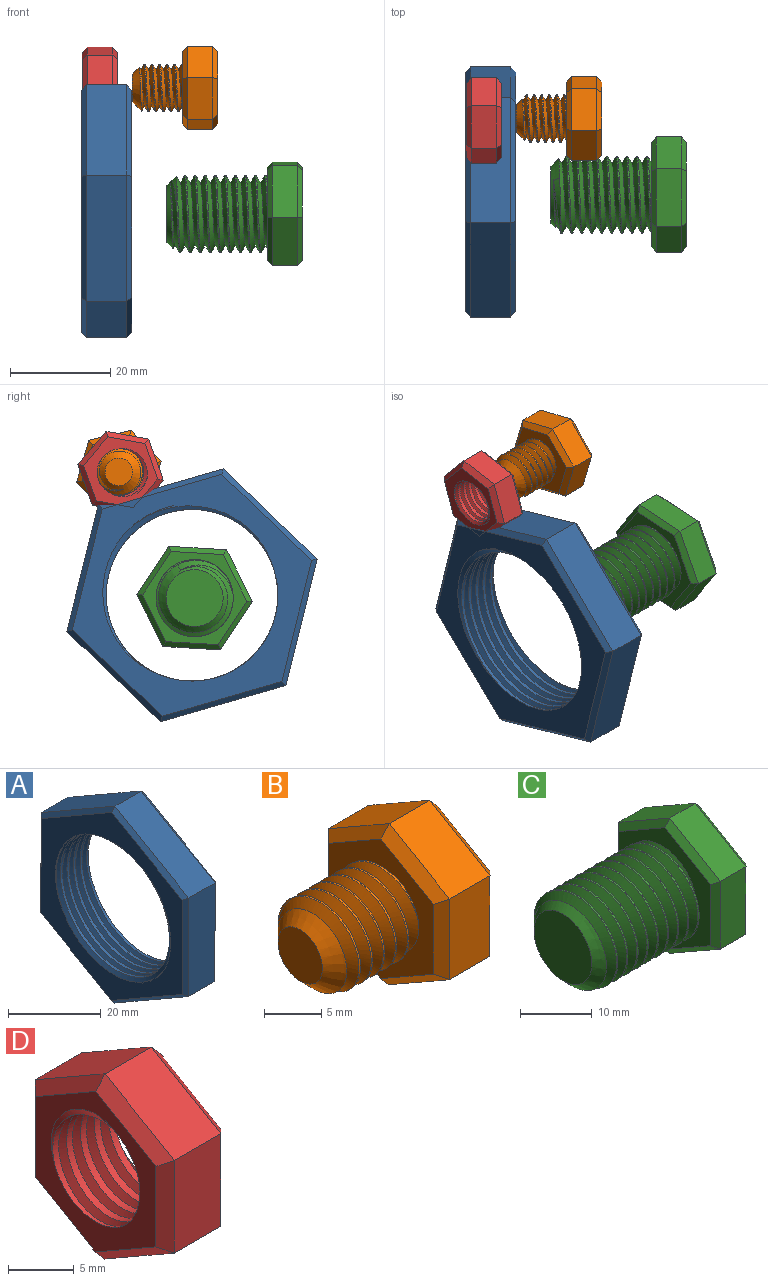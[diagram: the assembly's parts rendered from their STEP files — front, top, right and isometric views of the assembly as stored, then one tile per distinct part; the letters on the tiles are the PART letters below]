
ASSEMBLY  parts=4 mates=2
PART A: 23 faces, bbox 11.6x45x52 mm
  f0: cylinder r=17.12mm len=34.24mm, axis (1,0,0), area 378.5mm2, adj f7,f8,f21,f22
  f1: plane 22.48x13.02mm, normal (0,-0.5,0.87), area 207.8mm2, adj f2,f6,f14,f18
  f2: plane 25.98x8mm, normal (0,-1,0), area 207.8mm2, adj f1,f3,f12,f16
  f3: plane 22.52x12.96mm, normal (0,-0.5,-0.87), area 207.8mm2, adj f2,f4,f10,f15
  f4: plane 22.48x13.02mm, normal (0,0.5,-0.87), area 207.8mm2, adj f3,f5,f9,f17
  f5: plane 25.98x8mm, normal (0,1,0), area 207.8mm2, adj f4,f6,f11,f19
  f6: plane 22.52x12.96mm, normal (0,0.5,0.87), area 207.8mm2, adj f1,f5,f13,f20
  f7: plane 49.65x43.04mm, normal (-1,0,0), area 640.6mm2, adj f0,f9,f10,f11,f12,f13,f14,f21
  f8: plane 49.65x43.04mm, normal (1,0,0), area 640.6mm2, adj f0,f15,f16,f17,f18,f19,f20,f21
  f9: plane 22.48x13.6mm, normal (-0.71,0.35,-0.61), area 35.9mm2, adj f4,f7,f10,f11
  f10: plane 22.52x13.54mm, normal (-0.71,-0.35,-0.61), area 35.9mm2, adj f3,f7,f9,f12
  f11: plane 25.98x1.04mm, normal (-0.71,0.71,0), area 35.9mm2, adj f5,f7,f9,f13
  f12: plane 25.98x1.04mm, normal (-0.71,-0.71,0), area 35.9mm2, adj f2,f7,f10,f14
  f13: plane 22.52x13.54mm, normal (-0.71,0.35,0.61), area 35.9mm2, adj f6,f7,f11,f14
  f14: plane 22.48x13.6mm, normal (-0.71,-0.35,0.61), area 35.9mm2, adj f1,f7,f12,f13
  f15: plane 22.52x13.54mm, normal (0.71,-0.35,-0.61), area 35.9mm2, adj f3,f8,f16,f17
  f16: plane 25.98x1.04mm, normal (0.71,-0.71,0), area 35.9mm2, adj f2,f8,f15,f18
  f17: plane 22.48x13.6mm, normal (0.71,0.35,-0.61), area 35.9mm2, adj f4,f8,f15,f19
  f18: plane 22.48x13.6mm, normal (0.71,-0.35,0.61), area 35.9mm2, adj f1,f8,f16,f20
  f19: plane 25.98x1.04mm, normal (0.71,0.71,0), area 35.9mm2, adj f5,f8,f17,f20
  f20: plane 22.52x13.54mm, normal (0.71,0.35,0.61), area 35.9mm2, adj f6,f8,f18,f19
  f21: bspline ~42.13x36.49mm, area 721.4mm2, adj f0,f7,f8,f22
  f22: bspline ~42.13x36.49mm, area 721mm2, adj f0,f7,f8,f21
PART B: 25 faces, bbox 17.8x15.9x18.1 mm
  f0: cylinder r=4.75mm len=9.5mm, axis (1,0,0), area 28.1mm2, adj f1,f2,f4,f12
  f1: bspline ~10.97x9.91mm, area 196.7mm2, adj f0,f2,f4,f12
  f2: bspline ~10.97x10.66mm, area 196.6mm2, adj f0,f1,f4,f12
  f3: plane 5.5x5.5mm, normal (-1,0,0), area 23.8mm2, adj f4
  f4: cone r=4.75mm half-angle=45deg, axis (1,0,0), area 47.4mm2, adj f0,f1,f2,f3
  f5: plane 7.48x5mm, normal (0,-0.5,0.86), area 43.3mm2, adj f6,f10,f18,f22
  f6: plane 8.66x5mm, normal (0,-1,0), area 43.3mm2, adj f5,f7,f16,f20
  f7: plane 7.52x5mm, normal (0,-0.5,-0.87), area 43.3mm2, adj f6,f8,f14,f19
  f8: plane 7.48x5mm, normal (0,0.5,-0.86), area 43.3mm2, adj f7,f9,f13,f21
  f9: plane 8.66x5mm, normal (0,1,0), area 43.3mm2, adj f8,f10,f15,f23
  f10: plane 7.52x5mm, normal (0,0.5,0.87), area 43.3mm2, adj f5,f9,f17,f24
  f11: plane 15.01x13.03mm, normal (1,0,0), area 146.4mm2, adj f13,f14,f15,f16,f17,f18
  f12: plane 15.83x13.85mm, normal (-1,0,0), area 89.2mm2, adj f0,f1,f2,f19,f20,f21,f22,f23
  f13: plane 7.49x4.93mm, normal (0.71,0.36,-0.61), area 11.4mm2, adj f8,f11,f14,f15
  f14: plane 7.52x4.88mm, normal (0.71,-0.35,-0.61), area 11.4mm2, adj f7,f11,f13,f16
  f15: plane 8.66x1.03mm, normal (0.71,0.71,0), area 11.4mm2, adj f9,f11,f13,f17
  f16: plane 8.66x1.03mm, normal (0.71,-0.71,0), area 11.4mm2, adj f6,f11,f14,f18
  f17: plane 7.52x4.88mm, normal (0.71,0.35,0.61), area 11.4mm2, adj f10,f11,f15,f18
  f18: plane 7.49x4.93mm, normal (0.71,-0.36,0.61), area 11.4mm2, adj f5,f11,f16,f17
  f19: plane 7.52x4.88mm, normal (-0.71,-0.35,-0.61), area 11.4mm2, adj f7,f12,f20,f21
  f20: plane 8.66x1.03mm, normal (-0.71,-0.71,0), area 11.4mm2, adj f6,f12,f19,f22
  f21: plane 7.49x4.93mm, normal (-0.71,0.36,-0.61), area 11.4mm2, adj f8,f12,f19,f23
  f22: plane 7.49x4.93mm, normal (-0.71,-0.36,0.61), area 11.4mm2, adj f5,f12,f20,f24
  f23: plane 8.66x1.03mm, normal (-0.71,0.71,0), area 11.4mm2, adj f9,f12,f21,f24
  f24: plane 7.52x4.88mm, normal (-0.71,0.35,0.61), area 11.4mm2, adj f10,f12,f22,f23
PART C: 26 faces, bbox 27.7x20x23.1 mm
  f0: cylinder r=7.68mm len=18mm, axis (1,0,0), area 139.1mm2, adj f1,f2,f5,f13
  f1: bspline ~20.88x17.74mm, area 713.8mm2, adj f0,f2,f4,f5,f13
  f2: bspline ~21.88x17.74mm, area 715.1mm2, adj f0,f1,f4,f5,f13
  f3: plane 11.36x11.36mm, normal (-1,0,0), area 101.4mm2, adj f4
  f4: cone r=7.68mm half-angle=45deg, axis (1,0,0), area 63.2mm2, adj f1,f2,f3,f5
  f5: cone r=7.68mm half-angle=45deg, axis (1,0,0), area 13.2mm2, adj f0,f1,f2,f4
  f6: plane 9.98x5.81mm, normal (0,-0.5,0.86), area 57.7mm2, adj f7,f11,f19,f23
  f7: plane 11.55x5mm, normal (0,-1,0), area 57.7mm2, adj f6,f8,f17,f21
  f8: plane 10.02x5.74mm, normal (0,-0.5,-0.87), area 57.7mm2, adj f7,f9,f15,f20
  f9: plane 9.98x5.81mm, normal (0,0.5,-0.86), area 57.7mm2, adj f8,f10,f14,f22
  f10: plane 11.55x5mm, normal (0,1,0), area 57.7mm2, adj f9,f11,f16,f24
  f11: plane 10.02x5.74mm, normal (0,0.5,0.87), area 57.7mm2, adj f6,f10,f18,f25
  f12: plane 20.78x18.04mm, normal (1,0,0), area 280.6mm2, adj f14,f15,f16,f17,f18,f19
  f13: plane 20.78x18.04mm, normal (-1,0,0), area 125.2mm2, adj f0,f1,f2,f20,f21,f22,f23,f24
  f14: plane 9.98x6.38mm, normal (0.71,0.36,-0.61), area 15.5mm2, adj f9,f12,f15,f16
  f15: plane 10.02x6.32mm, normal (0.71,-0.35,-0.61), area 15.5mm2, adj f8,f12,f14,f17
  f16: plane 11.55x1.04mm, normal (0.71,0.71,0), area 15.5mm2, adj f10,f12,f14,f18
  f17: plane 11.55x1.04mm, normal (0.71,-0.71,0), area 15.5mm2, adj f7,f12,f15,f19
  f18: plane 10.02x6.32mm, normal (0.71,0.35,0.61), area 15.5mm2, adj f11,f12,f16,f19
  f19: plane 9.98x6.38mm, normal (0.71,-0.36,0.61), area 15.5mm2, adj f6,f12,f17,f18
  f20: plane 10.02x6.32mm, normal (-0.71,-0.35,-0.61), area 15.5mm2, adj f8,f13,f21,f22
  f21: plane 11.55x1.04mm, normal (-0.71,-0.71,0), area 15.5mm2, adj f7,f13,f20,f23
  f22: plane 9.98x6.38mm, normal (-0.71,0.36,-0.61), area 15.5mm2, adj f9,f13,f20,f24
  f23: plane 9.98x6.38mm, normal (-0.71,-0.36,0.61), area 15.5mm2, adj f6,f13,f21,f25
  f24: plane 11.55x1.04mm, normal (-0.71,0.71,0), area 15.5mm2, adj f10,f13,f22,f25
  f25: plane 10.02x6.32mm, normal (-0.71,0.35,0.61), area 15.5mm2, adj f11,f13,f23,f24
PART D: 23 faces, bbox 9.1x15.4x17.7 mm
  f0: plane 7.49x5mm, normal (0,-0.5,0.86), area 43.3mm2, adj f1,f5,f13,f17
  f1: plane 8.66x5mm, normal (0,-1,0), area 43.3mm2, adj f0,f2,f11,f15
  f2: plane 7.51x5mm, normal (0,-0.5,-0.87), area 43.3mm2, adj f1,f3,f9,f14
  f3: plane 7.49x5mm, normal (0,0.5,-0.86), area 43.3mm2, adj f2,f4,f8,f16
  f4: plane 8.66x5mm, normal (0,1,0), area 43.3mm2, adj f3,f5,f10,f18
  f5: plane 7.51x5mm, normal (0,0.5,0.87), area 43.3mm2, adj f0,f4,f12,f19
  f6: plane 15.37x13.38mm, normal (-1,0,0), area 71.4mm2, adj f8,f9,f10,f11,f12,f13,f20,f21
  f7: plane 15.37x13.38mm, normal (1,0,0), area 71.4mm2, adj f14,f15,f16,f17,f18,f19,f20,f21
  f8: plane 7.49x4.93mm, normal (-0.71,0.36,-0.61), area 11.4mm2, adj f3,f6,f9,f10
  f9: plane 7.51x4.89mm, normal (-0.71,-0.35,-0.61), area 11.4mm2, adj f2,f6,f8,f11
  f10: plane 8.66x1.02mm, normal (-0.71,0.71,0), area 11.4mm2, adj f4,f6,f8,f12
  f11: plane 8.66x1.02mm, normal (-0.71,-0.71,0), area 11.4mm2, adj f1,f6,f9,f13
  f12: plane 7.51x4.89mm, normal (-0.71,0.35,0.61), area 11.4mm2, adj f5,f6,f10,f13
  f13: plane 7.49x4.93mm, normal (-0.71,-0.36,0.61), area 11.4mm2, adj f0,f6,f11,f12
  f14: plane 7.51x4.89mm, normal (0.71,-0.35,-0.61), area 11.4mm2, adj f2,f7,f15,f16
  f15: plane 8.66x1.02mm, normal (0.71,-0.71,0), area 11.4mm2, adj f1,f7,f14,f17
  f16: plane 7.49x4.93mm, normal (0.71,0.36,-0.61), area 11.4mm2, adj f3,f7,f14,f18
  f17: plane 7.49x4.93mm, normal (0.71,-0.36,0.61), area 11.4mm2, adj f0,f7,f15,f19
  f18: plane 8.66x1.02mm, normal (0.71,0.71,0), area 11.4mm2, adj f4,f7,f16,f19
  f19: plane 7.51x4.89mm, normal (0.71,0.35,0.61), area 11.4mm2, adj f5,f7,f17,f18
  f20: cylinder r=4.66mm len=9.32mm, axis (1,0,0), area 85.4mm2, adj f6,f7,f21,f22
  f21: bspline ~12.5x10.82mm, area 128.4mm2, adj f6,f7,f20,f22
  f22: bspline ~12.5x10.82mm, area 128.5mm2, adj f6,f7,f20,f21
PLACE A rot(axis=(0,0.6,-0.8),180deg) t=(-55.27,-6.86,23.48)mm fixed
PLACE B rot(axis=(-1,0,0),43.8deg) t=(-31.66,7.73,48.08)mm
PLACE C rot(axis=(1,0,0),153.1deg) t=(-14.77,-7.38,22.92)mm
PLACE D rot(axis=(1,0,0),100.2deg) t=(-48.16,7.38,48.02)mm fixed
MATE cylindrical C.f0 <-> A.f7  axis (-1,0,0) through (-38.27,-7.38,22.92)mm
MATE cylindrical B.f0 <-> D.f6  axis (-1,0,0) through (-45.16,7.73,48.08)mm
